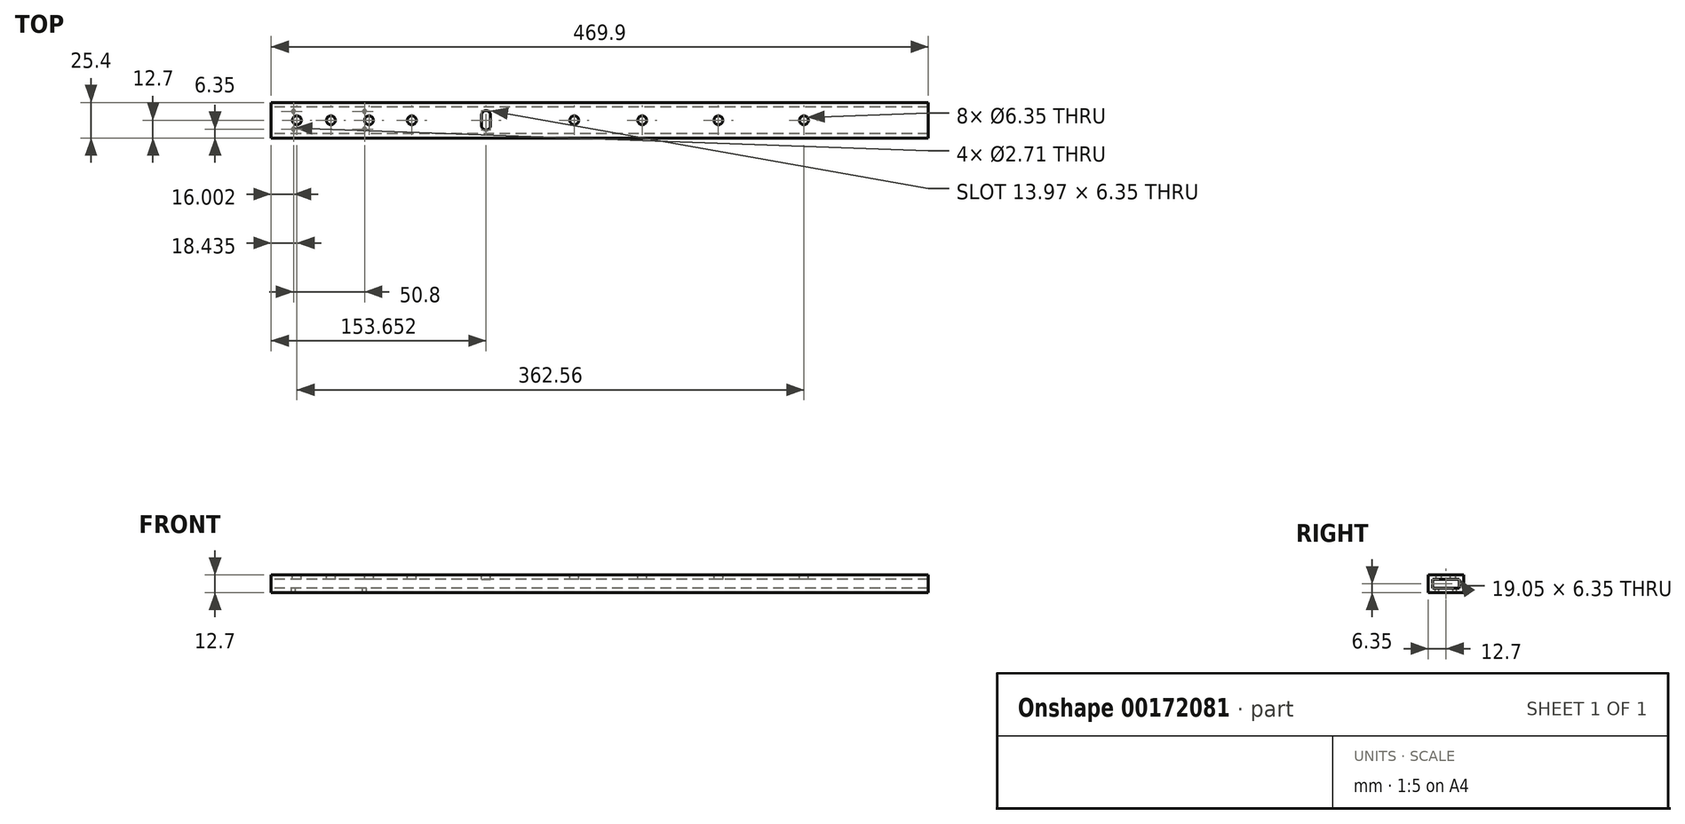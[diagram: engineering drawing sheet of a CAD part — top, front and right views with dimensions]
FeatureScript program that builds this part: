
annotation { "Feature Type Name" : "Feature", "Feature Type Description" : "" }
export const myFeature = defineFeature(function(context is Context, id is Id, definition is map)
    precondition{}
    {
        {
            var Q0;
            Q0=qCreatedBy(makeId("Right.planeOp"),FACE);
            var sketch = newSketch(context, id + "F0", { "sketchPlane" : qUnion([Q0])});
            skLineSegment(sketch, "E0.bottom", {"start": v(-12.7, 6.35) * mm, "end": v(12.7, 6.35) * mm});
            skLineSegment(sketch, "E0.top", {"start": v(-12.7, -6.35) * mm, "end": v(12.7, -6.35) * mm});
            skLineSegment(sketch, "E0.left", {"start": v(-12.7, 6.35) * mm, "end": v(-12.7, -6.35) * mm});
            skLineSegment(sketch, "E0.right", {"start": v(12.7, 6.35) * mm, "end": v(12.7, -6.35) * mm});
            skPoint(sketch, "E0.middle", {"position": v(0, 0) * mm});
            skLineSegment(sketch, "E1.bottom", {"start": v(-9.52, 3.18) * mm, "end": v(9.52, 3.18) * mm});
            skLineSegment(sketch, "E1.top", {"start": v(-9.52, -3.18) * mm, "end": v(9.52, -3.18) * mm});
            skLineSegment(sketch, "E1.left", {"start": v(-9.52, 3.18) * mm, "end": v(-9.52, -3.18) * mm});
            skLineSegment(sketch, "E1.right", {"start": v(9.52, 3.18) * mm, "end": v(9.52, -3.18) * mm});
            skSolve(sketch);
        }
        {
            var Q0;
            Q0=qSketchRegion(id+"F0",true);
            extrude(context, id + "F1", {"entities" : qUnion([Q0]), "depth" : 469.9 * mm, "offsetDistance" : 25.4 * mm});
        }
        {
            var Q0;
            Q0=makeQuery(id+"F1.opExtrude","SWEPT_FACE",FACE,{"disambiguationData":[OSD([sQuery(id+"F0.wireOp",EDGE,"E0.top")])]});
            var sketch = newSketch(context, id + "F2", { "sketchPlane" : qUnion([Q0])});
            skPoint(sketch, "E2", {"position": v(466.73, 6.35) * mm});
            skPoint(sketch, "E3", {"position": v(466.73, -6.35) * mm});
            skLineSegment(sketch, "E4", {"start": v(463.55, 0) * mm, "end": v(469.9, 0) * mm, "construction": true});
            skLineSegment(sketch, "E5", {"start": v(466.73, 0) * mm, "end": v(466.73, 6.35) * mm, "construction": true});
            skSolve(sketch);
        }
        {
            var Q0;
            Q0=makeQuery(id+"F1.opExtrude","SWEPT_FACE",FACE,{"disambiguationData":[OSD([sQuery(id+"F0.wireOp",EDGE,"E0.top")])]});
            var sketch = newSketch(context, id + "F3", { "sketchPlane" : qUnion([Q0])});
            skLineSegment(sketch, "E6", {"start": v(0, 0) * mm, "end": v(27.48, 0) * mm, "construction": true});
            skPoint(sketch, "E6.endSnap0", {"position": v(0, 0) * mm});
            skPoint(sketch, "E7", {"position": v(16, -6.35) * mm});
            skPoint(sketch, "E8", {"position": v(66.8, -6.35) * mm});
            skPoint(sketch, "E9", {"position": v(16, 6.35) * mm});
            skPoint(sketch, "E10", {"position": v(66.8, 6.35) * mm});
            skSolve(sketch);
        }
        {
            var Q0;
            Q0=sQuery(id+"F3.wireOp",VERTEX,"E7");
            var Q1;
            Q1=sQuery(id+"F3.wireOp",VERTEX,"E9");
            var Q2;
            Q2=sQuery(id+"F3.wireOp",VERTEX,"E10");
            var Q3;
            Q3=sQuery(id+"F3.wireOp",VERTEX,"E8");
            var Q4;
            Q4=makeQuery(id+"F1.opExtrude","SWEPT_BODY",BODY,{"disambiguationData":[OSD([sQuery(id+"F0.wireOp",EDGE,"E0.bottom"),sQuery(id+"F0.wireOp",EDGE,"E0.top"),sQuery(id+"F0.wireOp",EDGE,"E0.left"),sQuery(id+"F0.wireOp",EDGE,"E0.right"),sQuery(id+"F0.wireOp",EDGE,"E1.bottom"),sQuery(id+"F0.wireOp",EDGE,"E1.top"),sQuery(id+"F0.wireOp",EDGE,"E1.left"),sQuery(id+"F0.wireOp",EDGE,"E1.right")])]});
            hole(context, id + "F4", {"style" : HoleStyle.SIMPLE, "endStyle" : HoleEndStyle.BLIND, "standardTappedOrClearance" : lookupTablePath({ "standard" : "ANSI", "fit" : "Close (ASME)", "engagement" : "75%", "pitch" : "32 tpi", "size" : "#6", "type" : "Tapped" }), "standardBlindInLast" : lookupTablePath({ "fit" : "Close", "standard" : "ANSI", "engagement" : "75%", "pitch" : "32 tpi", "size" : "#6", "type" : "Tapped" }), "holeDiameter" : 2.7 * mm, "holeDepth" : 3.17 * mm, "locations" : qUnion([Q0, Q1, Q2, Q3]), "scope" : qUnion([Q4]), "majorDiameter" : 3.5 * mm, "startStyle" : HoleStartStyle.PART});
        }
        {
            var Q0;
            Q0=makeQuery(id+"F1.opExtrude","SWEPT_FACE",FACE,{"disambiguationData":[OSD([sQuery(id+"F0.wireOp",EDGE,"E0.bottom")])]});
            var sketch = newSketch(context, id + "F5", { "sketchPlane" : qUnion([Q0])});
            skCircle(sketch, "E11", {"center": v(381, 0) * mm, "radius": 3.18 * mm});
            skCircle(sketch, "E12", {"center": v(319.82, 0) * mm, "radius": 3.18 * mm});
            skCircle(sketch, "E13", {"center": v(265.31, 0) * mm, "radius": 3.18 * mm});
            skCircle(sketch, "E14", {"center": v(216.75, 0) * mm, "radius": 3.18 * mm});
            skLineSegment(sketch, "E15", {"start": v(153.65, 0) * mm, "end": v(153.65, -3.8) * mm, "construction": true});
            skArc(sketch, "E16", {"start": v(150.48, -3.8) * mm, "mid": v(153.65, -6.98) * mm, "end": v(156.83, -3.8) * mm});
            skArc(sketch, "E17.MirrorC", {"start": v(150.48, 3.81) * mm, "mid": v(153.65, 6.99) * mm, "end": v(156.83, 3.81) * mm});
            skCircle(sketch, "E18", {"center": v(100.6, 0) * mm, "radius": 3.18 * mm});
            skCircle(sketch, "E19", {"center": v(69.98, 0) * mm, "radius": 3.18 * mm});
            skCircle(sketch, "E20", {"center": v(42.73, 0) * mm, "radius": 3.18 * mm});
            skCircle(sketch, "E21", {"center": v(18.43, 0) * mm, "radius": 3.18 * mm});
            skLineSegment(sketch, "E22", {"start": v(150.48, -3.8) * mm, "end": v(150.48, 3.81) * mm});
            skLineSegment(sketch, "E23", {"start": v(156.83, 3.81) * mm, "end": v(156.83, -3.8) * mm});
            skLineSegment(sketch, "E24", {"start": v(469.9, 0) * mm, "end": v(18.43, 0) * mm, "construction": true});
            skPoint(sketch, "E25", {"position": v(469.9, 0) * mm});
            skSolve(sketch);
        }
        {
            var Q0;
            Q0 = qSketchRegion(id + "F5", true);
            extrude(context, id + "F6", {"entities" : qUnion([Q0]), "operationType" : NewBodyOperationType.REMOVE, "oppositeDirection" : true, "depth" : 3.17 * mm});
        }
    });
